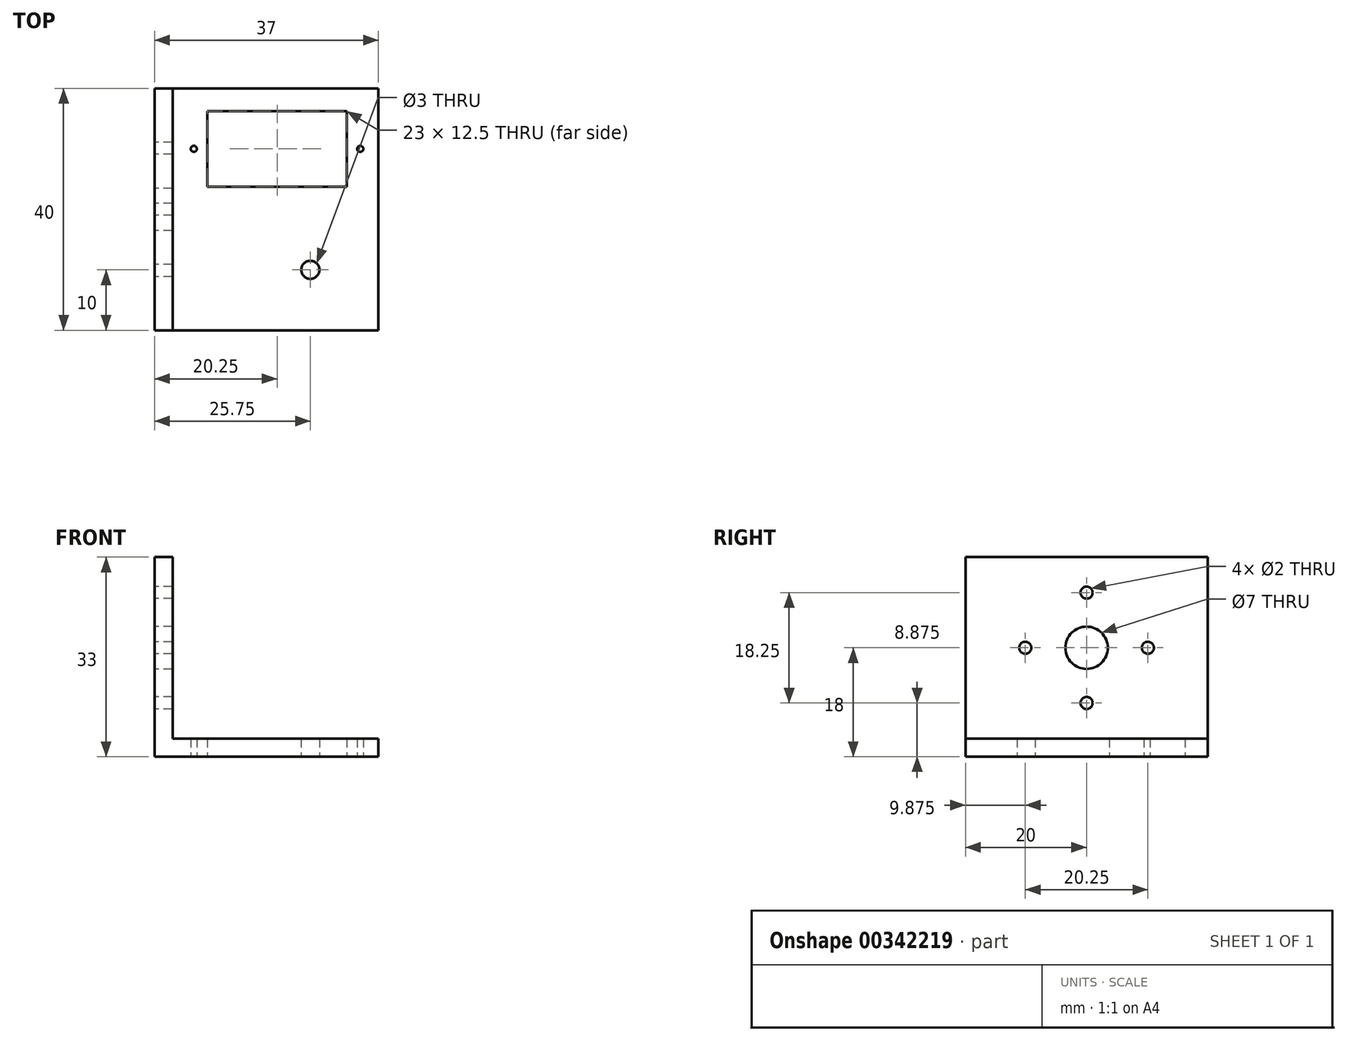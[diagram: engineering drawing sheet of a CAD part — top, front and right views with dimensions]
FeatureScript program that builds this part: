
annotation { "Feature Type Name" : "Feature", "Feature Type Description" : "" }
export const myFeature = defineFeature(function(context is Context, id is Id, definition is map)
    precondition{}
    {
        {
            var Q0;
            Q0=qCreatedBy(makeId("Top.planeOp"),FACE);
            var sketch = newSketch(context, id + "F0", { "sketchPlane" : qUnion([Q0])});
            skLineSegment(sketch, "E0", {"start": v(8.75, 36.25) * mm, "end": v(8.75, 23.75) * mm});
            skLineSegment(sketch, "E1", {"start": v(8.75, 23.75) * mm, "end": v(31.75, 23.75) * mm});
            skLineSegment(sketch, "E2", {"start": v(31.75, 36.25) * mm, "end": v(8.75, 36.25) * mm});
            skCircle(sketch, "E3", {"center": v(34, 30) * mm, "radius": 0.5 * mm});
            skPoint(sketch, "E4.visualSharp", {"position": v(3, 40) * mm});
            skPoint(sketch, "E5.visualSharp", {"position": v(37, 40) * mm});
            skPoint(sketch, "E6.visualSharp", {"position": v(37, 0) * mm});
            skPoint(sketch, "E7.visualSharp", {"position": v(3, 0) * mm});
            skLineSegment(sketch, "E8", {"start": v(3, 40) * mm, "end": v(37, 40) * mm});
            skLineSegment(sketch, "E9", {"start": v(37, 0) * mm, "end": v(37, 40) * mm});
            skLineSegment(sketch, "E10", {"start": v(37, 0) * mm, "end": v(3, 0) * mm});
            skLineSegment(sketch, "E11", {"start": v(3, 0) * mm, "end": v(3, 40) * mm});
            skCircle(sketch, "E12.MirrorC", {"center": v(6.5, 30) * mm, "radius": 0.5 * mm});
            skLineSegment(sketch, "E13", {"start": v(31.75, 36.25) * mm, "end": v(31.75, 23.75) * mm});
            skLineSegment(sketch, "E14", {"start": v(3, 0) * mm, "end": v(0, 0) * mm});
            skLineSegment(sketch, "E15", {"start": v(0, 0) * mm, "end": v(0, 40) * mm});
            skLineSegment(sketch, "E16", {"start": v(0, 40) * mm, "end": v(3, 40) * mm});
            skLineSegment(sketch, "E17", {"start": v(8.75, 23.75) * mm, "end": v(14.75, 23.75) * mm});
            skLineSegment(sketch, "E18", {"start": v(14.75, 23.75) * mm, "end": v(14.75, 10) * mm, "construction": true});
            skCircle(sketch, "E19", {"center": v(14.75, 10) * mm, "radius": 1.5 * mm, "construction": true});
            skCircle(sketch, "E20.MirrorC", {"center": v(25.75, 10) * mm, "radius": 1.5 * mm});
            skLineSegment(sketch, "E21.MirrorCS", {"start": v(25.75, 23.75) * mm, "end": v(25.75, 10) * mm});
            skSolve(sketch);
        }
        {
            var Q0;
            Q0=makeQuery(id+"F0.imprint","IMPRINT",FACE,{"disambiguationData":[TD([[makeQuery(id+"F0.imprint","IMPRINT",EDGE,{"derivedFrom":sQuery(id+"F0.wireOp",EDGE,"E0")}),-1.0]])]});
            var Q1;
            Q1=makeQuery(id+"F0.imprint","IMPRINT",FACE,{"disambiguationData":[TD([[makeQuery(id+"F0.imprint","IMPRINT",EDGE,{"derivedFrom":sQuery(id+"F0.wireOp",EDGE,"E11")}),1.0]])]});
            extrude(context, id + "F1", {"entities" : qUnion([Q0, Q1]), "depth" : 3 * mm});
        }
        {
            var Q0;
            Q0=qCreatedBy(makeId("Right.planeOp"),FACE);
            var sketch = newSketch(context, id + "F2", { "sketchPlane" : qUnion([Q0])});
            skLineSegment(sketch, "E22", {"start": v(0, 0) * mm, "end": v(0, 3) * mm});
            skLineSegment(sketch, "E23", {"start": v(0, 3) * mm, "end": v(0, 33) * mm});
            skLineSegment(sketch, "E24", {"start": v(0, 33) * mm, "end": v(34, 33) * mm});
            skPoint(sketch, "E25.endSnap0", {"position": v(0, 18) * mm});
            skCircle(sketch, "E26", {"center": v(20, 18) * mm, "radius": 3.5 * mm});
            skLineSegment(sketch, "E27", {"start": v(20, 18) * mm, "end": v(20, 27.12) * mm});
            skLineSegment(sketch, "E28", {"start": v(16.5, 18) * mm, "end": v(30.12, 18) * mm});
            skLineSegment(sketch, "E29", {"start": v(23.31, 18) * mm, "end": v(9.87, 18) * mm});
            skLineSegment(sketch, "E30", {"start": v(20, 14.5) * mm, "end": v(20, 27.13) * mm});
            skLineSegment(sketch, "E31", {"start": v(20, 21.5) * mm, "end": v(20, 8.88) * mm});
            skCircle(sketch, "E32", {"center": v(30.12, 18) * mm, "radius": 1 * mm});
            skCircle(sketch, "E33", {"center": v(20, 27.13) * mm, "radius": 1 * mm});
            skCircle(sketch, "E34", {"center": v(9.87, 18) * mm, "radius": 1 * mm});
            skCircle(sketch, "E35", {"center": v(20, 8.88) * mm, "radius": 1 * mm});
            skLineSegment(sketch, "E36", {"start": v(0, 0) * mm, "end": v(20, 0) * mm});
            skLineSegment(sketch, "E37", {"start": v(20, 0) * mm, "end": v(40, 0) * mm});
            skLineSegment(sketch, "E38", {"start": v(40, 0) * mm, "end": v(40, 30) * mm});
            skLineSegment(sketch, "E39", {"start": v(40, 30) * mm, "end": v(40, 33) * mm});
            skLineSegment(sketch, "E40", {"start": v(40, 33) * mm, "end": v(34, 33) * mm});
            skLineSegment(sketch, "E41", {"start": v(20, 18) * mm, "end": v(20, 0) * mm});
            skSolve(sketch);
        }
        {
            var Q0;
            {var subQ8=sQuery(id+"F2.wireOp",EDGE,"E23");Q0=makeQuery(id+"F2.imprint","IMPRINT",FACE,{"disambiguationData":[TD([[makeQuery(id+"F2.imprint","IMPRINT",EDGE,{"derivedFrom":subQ8}),-1.0]])]});}
            extrude(context, id + "F3", {"entities" : qUnion([Q0]), "operationType" : NewBodyOperationType.ADD, "depth" : 3 * mm});
        }
    });
